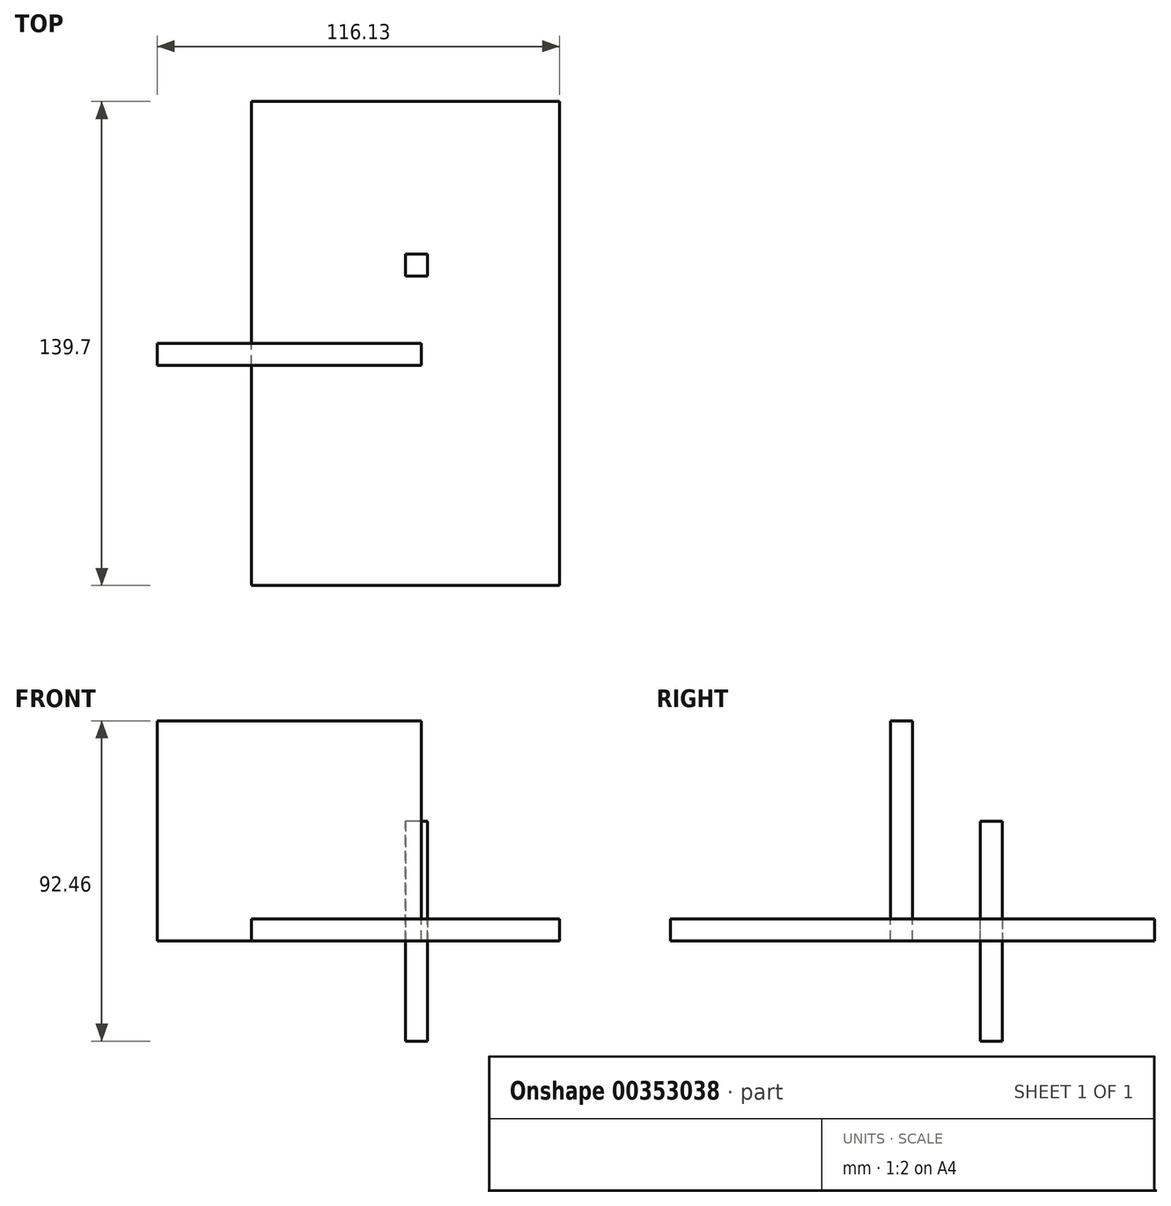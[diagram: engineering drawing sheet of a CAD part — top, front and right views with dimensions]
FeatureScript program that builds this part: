
annotation { "Feature Type Name" : "Feature", "Feature Type Description" : "" }
export const myFeature = defineFeature(function(context is Context, id is Id, definition is map)
    precondition{}
    {
        {
            var Q0;
            Q0=qCreatedBy(makeId("Top.planeOp"),FACE);
            var sketch = newSketch(context, id + "F0", { "sketchPlane" : qUnion([Q0])});
            skLineSegment(sketch, "E0", {"start": v(0, 0) * mm, "end": v(-38.1, 0) * mm});
            skLineSegment(sketch, "E1", {"start": v(-38.1, 0) * mm, "end": v(38.1, 0) * mm});
            skLineSegment(sketch, "E2", {"start": v(38.1, 0) * mm, "end": v(38.1, 63.5) * mm});
            skLineSegment(sketch, "E3", {"start": v(38.1, 0) * mm, "end": v(38.1, -63.5) * mm});
            skLineSegment(sketch, "E4.bottom", {"start": v(38.1, 63.5) * mm, "end": v(-38.1, 63.5) * mm});
            skLineSegment(sketch, "E4.top", {"start": v(38.1, -63.5) * mm, "end": v(-38.1, -63.5) * mm});
            skLineSegment(sketch, "E4.left", {"start": v(38.1, 63.5) * mm, "end": v(38.1, -63.5) * mm});
            skLineSegment(sketch, "E4.right", {"start": v(-38.1, 63.5) * mm, "end": v(-38.1, -63.5) * mm});
            skLineSegment(sketch, "E5", {"start": v(-38.1, 0) * mm, "end": v(-44.45, 0) * mm});
            skLineSegment(sketch, "E6", {"start": v(38.1, 0) * mm, "end": v(44.45, 0) * mm});
            skLineSegment(sketch, "E7", {"start": v(0, 63.5) * mm, "end": v(0, 69.85) * mm});
            skLineSegment(sketch, "E8", {"start": v(0, -63.5) * mm, "end": v(0, -69.85) * mm});
            skPoint(sketch, "E8.endSnap0", {"position": v(0, -63.5) * mm});
            skLineSegment(sketch, "E9.bottom", {"start": v(44.45, -69.85) * mm, "end": v(-44.45, -69.85) * mm});
            skLineSegment(sketch, "E9.top", {"start": v(44.45, 69.85) * mm, "end": v(-44.45, 69.85) * mm});
            skLineSegment(sketch, "E9.left", {"start": v(44.45, -69.85) * mm, "end": v(44.45, 69.85) * mm});
            skLineSegment(sketch, "E9.right", {"start": v(-44.45, -69.85) * mm, "end": v(-44.45, 69.85) * mm});
            skLineSegment(sketch, "E10", {"start": v(-44.45, 69.85) * mm, "end": v(44.45, 69.85) * mm});
            skSolve(sketch);
        }
        {
            var Q0;
            Q0=qCreatedBy(makeId("Right.planeOp"),FACE);
            var sketch = newSketch(context, id + "F1", { "sketchPlane" : qUnion([Q0])});
            skLineSegment(sketch, "E11", {"start": v(152.85, -35.3) * mm, "end": v(152.85, 40.9) * mm});
            skLineSegment(sketch, "E12", {"start": v(152.85, 40.9) * mm, "end": v(152.85, 34.54) * mm});
            skLineSegment(sketch, "E13", {"start": v(152.85, 34.54) * mm, "end": v(152.85, -28.96) * mm});
            skLineSegment(sketch, "E14", {"start": v(152.85, 34.54) * mm, "end": v(25.85, 34.54) * mm});
            skLineSegment(sketch, "E15", {"start": v(25.85, 34.54) * mm, "end": v(25.85, -28.96) * mm});
            skLineSegment(sketch, "E16", {"start": v(25.85, -28.96) * mm, "end": v(25.85, -35.3) * mm});
            skLineSegment(sketch, "E17", {"start": v(25.85, -28.96) * mm, "end": v(152.85, -28.96) * mm});
            skLineSegment(sketch, "E18", {"start": v(25.85, -28.96) * mm, "end": v(19.5, -28.96) * mm});
            skLineSegment(sketch, "E19", {"start": v(152.85, 34.54) * mm, "end": v(159.2, 34.54) * mm});
            skLineSegment(sketch, "E20.bottom", {"start": v(19.5, -35.3) * mm, "end": v(159.2, -35.3) * mm});
            skLineSegment(sketch, "E20.top", {"start": v(19.5, 40.9) * mm, "end": v(159.2, 40.9) * mm});
            skLineSegment(sketch, "E20.left", {"start": v(19.5, -35.3) * mm, "end": v(19.5, 40.9) * mm});
            skLineSegment(sketch, "E20.right", {"start": v(159.2, -35.3) * mm, "end": v(159.2, 40.9) * mm});
            skLineSegment(sketch, "E21", {"start": v(25.85, 34.54) * mm, "end": v(19.5, 34.54) * mm});
            skLineSegment(sketch, "E22", {"start": v(152.85, -28.96) * mm, "end": v(159.2, -28.96) * mm});
            skSolve(sketch);
        }
        {
            var Q0;
            Q0=qCreatedBy(makeId("Front.planeOp"),FACE);
            var sketch = newSketch(context, id + "F2", { "sketchPlane" : qUnion([Q0])});
            skLineSegment(sketch, "E23.bottom", {"start": v(4.52, 0) * mm, "end": v(-71.68, 0) * mm});
            skLineSegment(sketch, "E23.top", {"start": v(4.52, 63.5) * mm, "end": v(-71.68, 63.5) * mm});
            skLineSegment(sketch, "E23.left", {"start": v(4.52, 0) * mm, "end": v(4.52, 63.5) * mm});
            skLineSegment(sketch, "E23.right", {"start": v(-71.68, 0) * mm, "end": v(-71.68, 63.5) * mm});
            skSolve(sketch);
        }
        {
            var Q0;
            Q0=makeQuery(id+"F2.imprint","IMPRINT",FACE,{"disambiguationData":[TD([[makeQuery(id+"F2.imprint","IMPRINT",EDGE,{"derivedFrom":sQuery(id+"F2.wireOp",EDGE,"E23.bottom")}),-1.0]])]});
            extrude(context, id + "F3", {"entities" : qUnion([Q0]), "depth" : 6.35 * mm});
        }
        {
            var Q0;
            Q0=makeQuery(id+"F1.imprint","IMPRINT",FACE,{"disambiguationData":[TD([[makeQuery(id+"F1.imprint","IMPRINT",EDGE,{"derivedFrom":sQuery(id+"F1.wireOp",EDGE,"E13")}),-1.0]])]});
            var Q1;
            Q1=makeQuery(id+"F1.imprint","IMPRINT",FACE,{"disambiguationData":[TD([[makeQuery(id+"F1.imprint","IMPRINT",EDGE,{"derivedFrom":sQuery(id+"F1.wireOp",EDGE,"E15")}),-1.0]])]});
            var Q2;
            Q2=makeQuery(id+"F1.imprint","IMPRINT",FACE,{"disambiguationData":[TD([[makeQuery(id+"F1.imprint","IMPRINT",EDGE,{"derivedFrom":sQuery(id+"F1.wireOp",EDGE,"E13")}),1.0]])]});
            extrude(context, id + "F4", {"entities" : qUnion([Q0, Q1, Q2]), "depth" : 6.35 * mm});
        }
        {
            var Q0;
            {var subQ1=sQuery(id+"F0.wireOp",EDGE,"E5");Q0=makeQuery(id+"F0.imprint","IMPRINT",FACE,{"disambiguationData":[TD([[makeQuery(id+"F0.imprint","IMPRINT",EDGE,{"derivedFrom":subQ1}),1.0]])]});}
            var Q1;
            {var subQ4=sQuery(id+"F0.wireOp",EDGE,"E1");var subQ6=makeQuery(id+"F0.imprint","IMPRINT",VERTEX,{"derivedFrom":subQ4});Q1=makeQuery(id+"F0.imprint","IMPRINT",FACE,{"disambiguationData":[TD([[makeQuery(id+"F0.imprint","IMPRINT",EDGE,{"disambiguationData":[TD([[subQ6,1.0]])],"derivedFrom":subQ4}),-1.0]])]});}
            var Q2;
            {var subQ1=sQuery(id+"F0.wireOp",EDGE,"E5");Q2=makeQuery(id+"F0.imprint","IMPRINT",FACE,{"disambiguationData":[TD([[makeQuery(id+"F0.imprint","IMPRINT",EDGE,{"derivedFrom":subQ1}),-1.0]])]});}
            var Q3;
            {var subQ6=sQuery(id+"F0.wireOp",EDGE,"E1");var subQ8=makeQuery(id+"F0.imprint","IMPRINT",VERTEX,{"derivedFrom":subQ6});Q3=makeQuery(id+"F0.imprint","IMPRINT",FACE,{"disambiguationData":[TD([[makeQuery(id+"F0.imprint","IMPRINT",EDGE,{"disambiguationData":[TD([[subQ8,1.0]])],"derivedFrom":subQ6}),1.0]])]});}
            var Q4;
            {var subQ0=sQuery(id+"F0.wireOp",EDGE,"E6");Q4=makeQuery(id+"F0.imprint","IMPRINT",FACE,{"disambiguationData":[TD([[makeQuery(id+"F0.imprint","IMPRINT",EDGE,{"derivedFrom":subQ0}),1.0]])]});}
            var Q5;
            {var subQ1=sQuery(id+"F0.wireOp",EDGE,"E6");Q5=makeQuery(id+"F0.imprint","IMPRINT",FACE,{"disambiguationData":[TD([[makeQuery(id+"F0.imprint","IMPRINT",EDGE,{"derivedFrom":subQ1}),-1.0]])]});}
            extrude(context, id + "F5", {"entities" : qUnion([Q0, Q1, Q2, Q3, Q4, Q5]), "depth" : 6.35 * mm});
        }
    });
